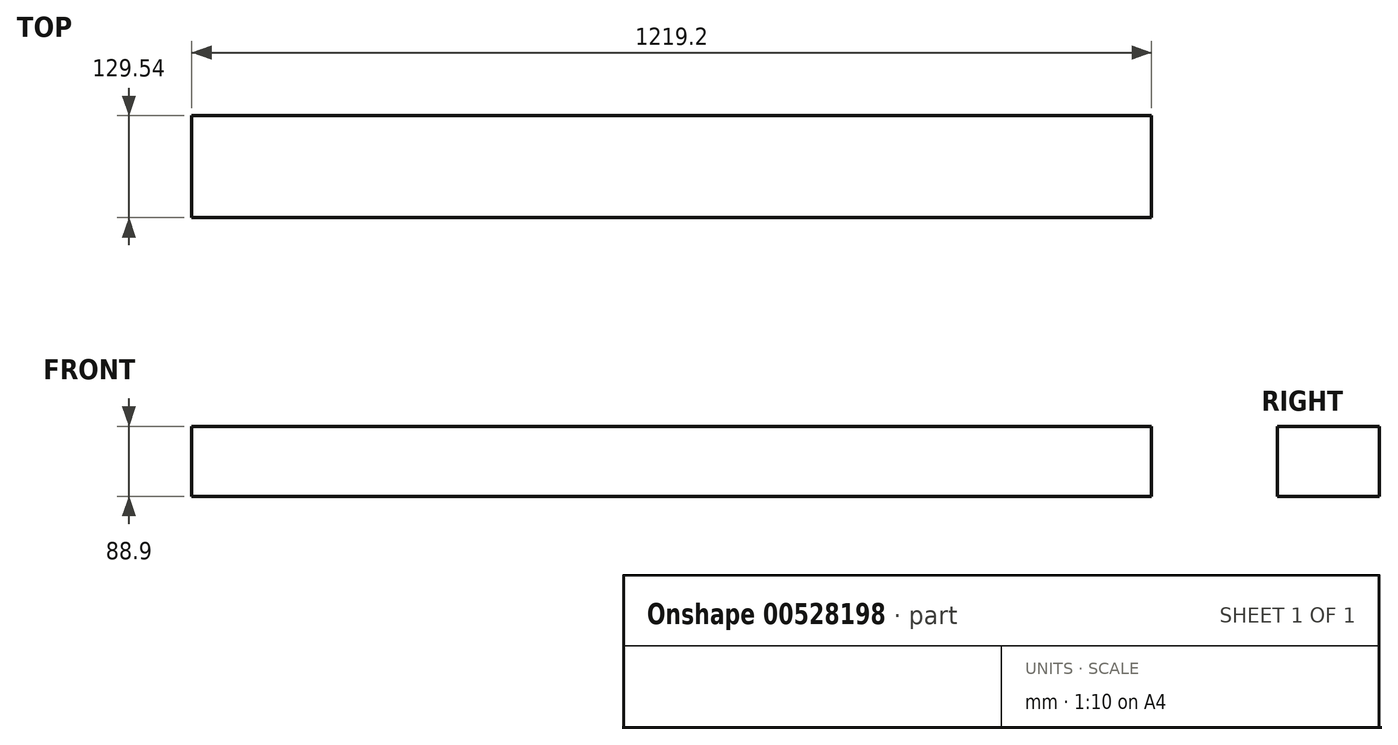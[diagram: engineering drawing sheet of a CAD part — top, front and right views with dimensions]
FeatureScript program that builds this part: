
annotation { "Feature Type Name" : "Feature", "Feature Type Description" : "" }
export const myFeature = defineFeature(function(context is Context, id is Id, definition is map)
    precondition{}
    {
        {
            var Q0;
            Q0=qCreatedBy(makeId("Top.planeOp"),FACE);
            var sketch = newSketch(context, id + "F0", { "sketchPlane" : qUnion([Q0])});
            skPoint(sketch, "E0.left.start.orphan", {"position": v(33.6, 0) * mm});
            skLineSegment(sketch, "E1.bottom", {"start": v(0, 0) * mm, "end": v(1219.2, 0) * mm});
            skLineSegment(sketch, "E1.top", {"start": v(0, 129.54) * mm, "end": v(1219.2, 129.54) * mm});
            skLineSegment(sketch, "E1.left", {"start": v(0, 0) * mm, "end": v(0, 129.54) * mm});
            skLineSegment(sketch, "E1.right", {"start": v(1219.2, 0) * mm, "end": v(1219.2, 129.54) * mm});
            skSolve(sketch);
        }
        {
            var Q0;
            Q0 = qSketchRegion(id + "F0", true);
            extrude(context, id + "F1", {"entities" : qUnion([Q0]), "depth" : 88.9 * mm, "offsetDistance" : 25.4 * mm});
        }
    });
